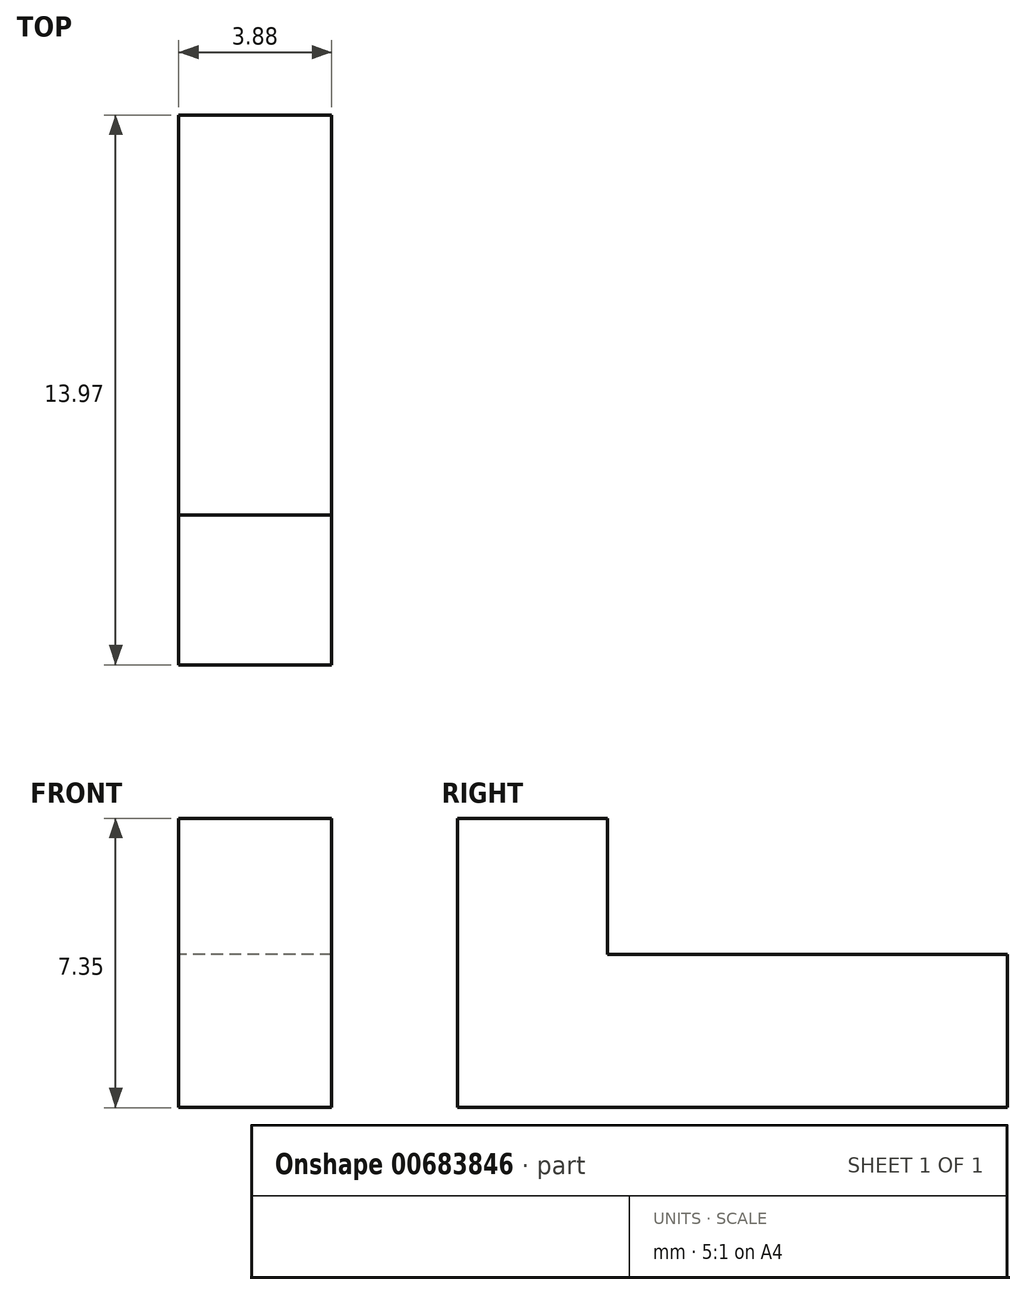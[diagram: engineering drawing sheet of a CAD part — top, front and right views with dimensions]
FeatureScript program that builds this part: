
annotation { "Feature Type Name" : "Feature", "Feature Type Description" : "" }
export const myFeature = defineFeature(function(context is Context, id is Id, definition is map)
    precondition{}
    {
        {
            var Q0;
            Q0=qCreatedBy(makeId("Front.planeOp"),FACE);
            var sketch = newSketch(context, id + "F0", { "sketchPlane" : qUnion([Q0])});
            skLineSegment(sketch, "E0.bottom", {"start": v(1.94, -1.95) * mm, "end": v(-1.94, -1.95) * mm});
            skLineSegment(sketch, "E0.top", {"start": v(1.94, 1.95) * mm, "end": v(-1.94, 1.95) * mm});
            skLineSegment(sketch, "E0.left", {"start": v(1.94, -1.95) * mm, "end": v(1.94, 1.95) * mm});
            skLineSegment(sketch, "E0.right", {"start": v(-1.94, -1.95) * mm, "end": v(-1.94, 1.95) * mm});
            skPoint(sketch, "E0.middle", {"position": v(0, 0) * mm});
            skSolve(sketch);
        }
        {
            var Q0;
            Q0=makeQuery(id+"F0.imprint","IMPRINT",FACE,{"disambiguationData":[TD([[makeQuery(id+"F0.imprint","IMPRINT",EDGE,{"derivedFrom":sQuery(id+"F0.wireOp",EDGE,"E0.bottom")}),-1.0]])]});
            extrude(context, id + "F1", {"entities" : qUnion([Q0]), "depth" : 5.08 * mm, "offsetDistance" : 25.4 * mm, "hasSecondDirection" : true, "secondDirectionOppositeDirection" : true, "secondDirectionDepth" : 5.08 * mm});
        }
        {
            var Q0;
            Q0=makeQuery(id+"F1.opExtrude","CAP_FACE",FACE,{"disambiguationData":[OSD([sQuery(id+"F0.wireOp",EDGE,"E0.bottom"),sQuery(id+"F0.wireOp",EDGE,"E0.top"),sQuery(id+"F0.wireOp",EDGE,"E0.left"),sQuery(id+"F0.wireOp",EDGE,"E0.right")])],"isStart":false});
            var sketch = newSketch(context, id + "F2", { "sketchPlane" : qUnion([Q0])});
            skLineSegment(sketch, "E1.bottom", {"start": v(-1.94, -1.95) * mm, "end": v(1.94, -1.95) * mm});
            skLineSegment(sketch, "E1.top", {"start": v(-1.94, 5.4) * mm, "end": v(1.94, 5.4) * mm});
            skLineSegment(sketch, "E1.left", {"start": v(-1.94, -1.95) * mm, "end": v(-1.94, 5.4) * mm});
            skLineSegment(sketch, "E1.right", {"start": v(1.94, -1.95) * mm, "end": v(1.94, 5.4) * mm});
            skSolve(sketch);
        }
        {
            var Q0;
            Q0 = qSketchRegion(id + "F2", true);
            extrude(context, id + "F3", {"entities" : qUnion([Q0]), "operationType" : NewBodyOperationType.ADD, "depth" : 3.8 * mm, "offsetDistance" : 25.4 * mm});
        }
    });
